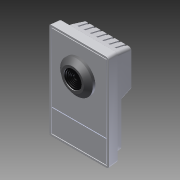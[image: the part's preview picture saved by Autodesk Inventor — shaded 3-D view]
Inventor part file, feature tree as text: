
AUTODESK INVENTOR PART (.ipt)
format: ipt  version: 2014 SP1 (Build 180222100, 222)  size: 780,288 bytes
history: native  units: in
note: dims shown in document units (in); Inventor stores cm internally (conversion verified against a paired STEP export)
features: fillet x1, other x1, thread x1, imported_body x1
ambient origin geometry x8: Origin, YZ Plane, XZ Plane, XY Plane, X Axis, Y Axis, Z Axis, Center Point
bodies: Body1 (feature_tree)
feature tree (4):
  fillet  "Fillet18"  Radius=1.0in
  other  "AXIS M10111"
  thread  "Thread1"  [1 undecoded]
  imported_body  "Base1"
note: 1 required parameter value undecoded (feature->parameter linkage not recoverable at this tier; creation-order binding heuristic only, values carry confidence <= 0.55)
